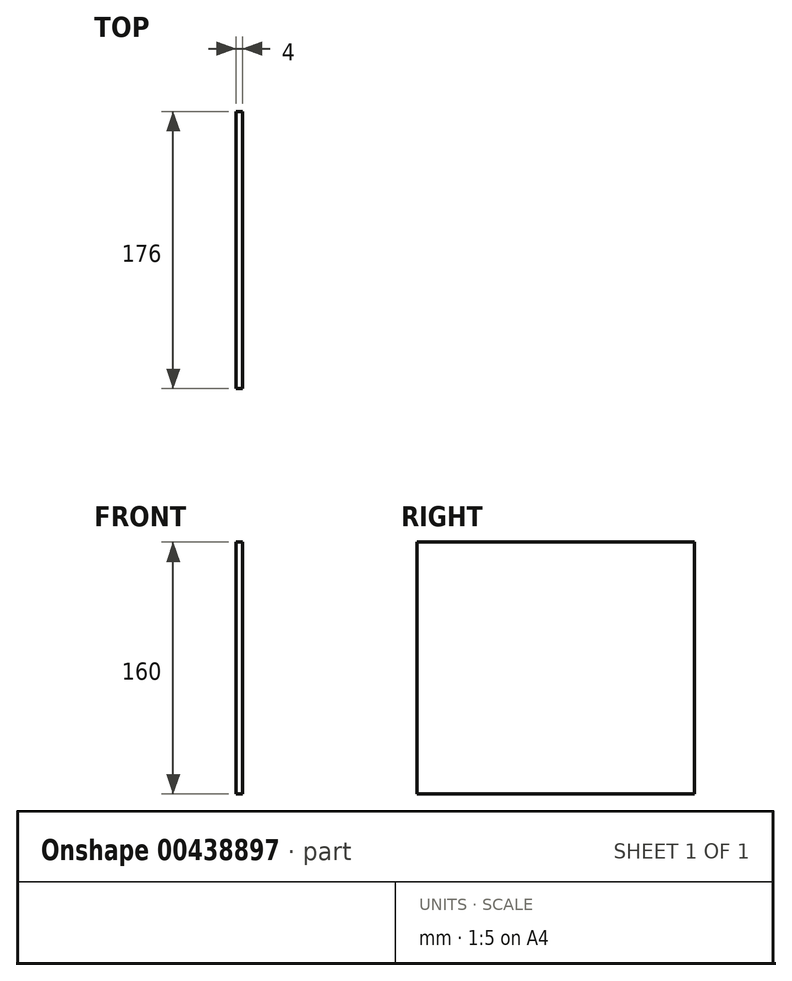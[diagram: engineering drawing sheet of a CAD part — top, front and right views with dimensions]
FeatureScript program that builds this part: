
annotation { "Feature Type Name" : "Feature", "Feature Type Description" : "" }
export const myFeature = defineFeature(function(context is Context, id is Id, definition is map)
    precondition{}
    {
        {
            var Q0;
            Q0=qCreatedBy(makeId("Right.planeOp"),FACE);
            var sketch = newSketch(context, id + "F0", { "sketchPlane" : qUnion([Q0])});
            skLineSegment(sketch, "E0", {"start": v(0, 160) * mm, "end": v(-176, 160) * mm});
            skLineSegment(sketch, "E1", {"start": v(-176, 160) * mm, "end": v(-176, 0) * mm});
            skLineSegment(sketch, "E2", {"start": v(-176, 0) * mm, "end": v(0, 0) * mm});
            skLineSegment(sketch, "E3", {"start": v(0, 0) * mm, "end": v(0, 160) * mm});
            skSolve(sketch);
        }
        {
            var Q0;
            Q0=makeQuery(id+"F0.imprint","IMPRINT",FACE,{"disambiguationData":[TD([[makeQuery(id+"F0.imprint","IMPRINT",EDGE,{"derivedFrom":sQuery(id+"F0.wireOp",EDGE,"E0")}),1.0]])]});
            extrude(context, id + "F1", {"entities" : qUnion([Q0]), "depth" : 4 * mm});
        }
    });
